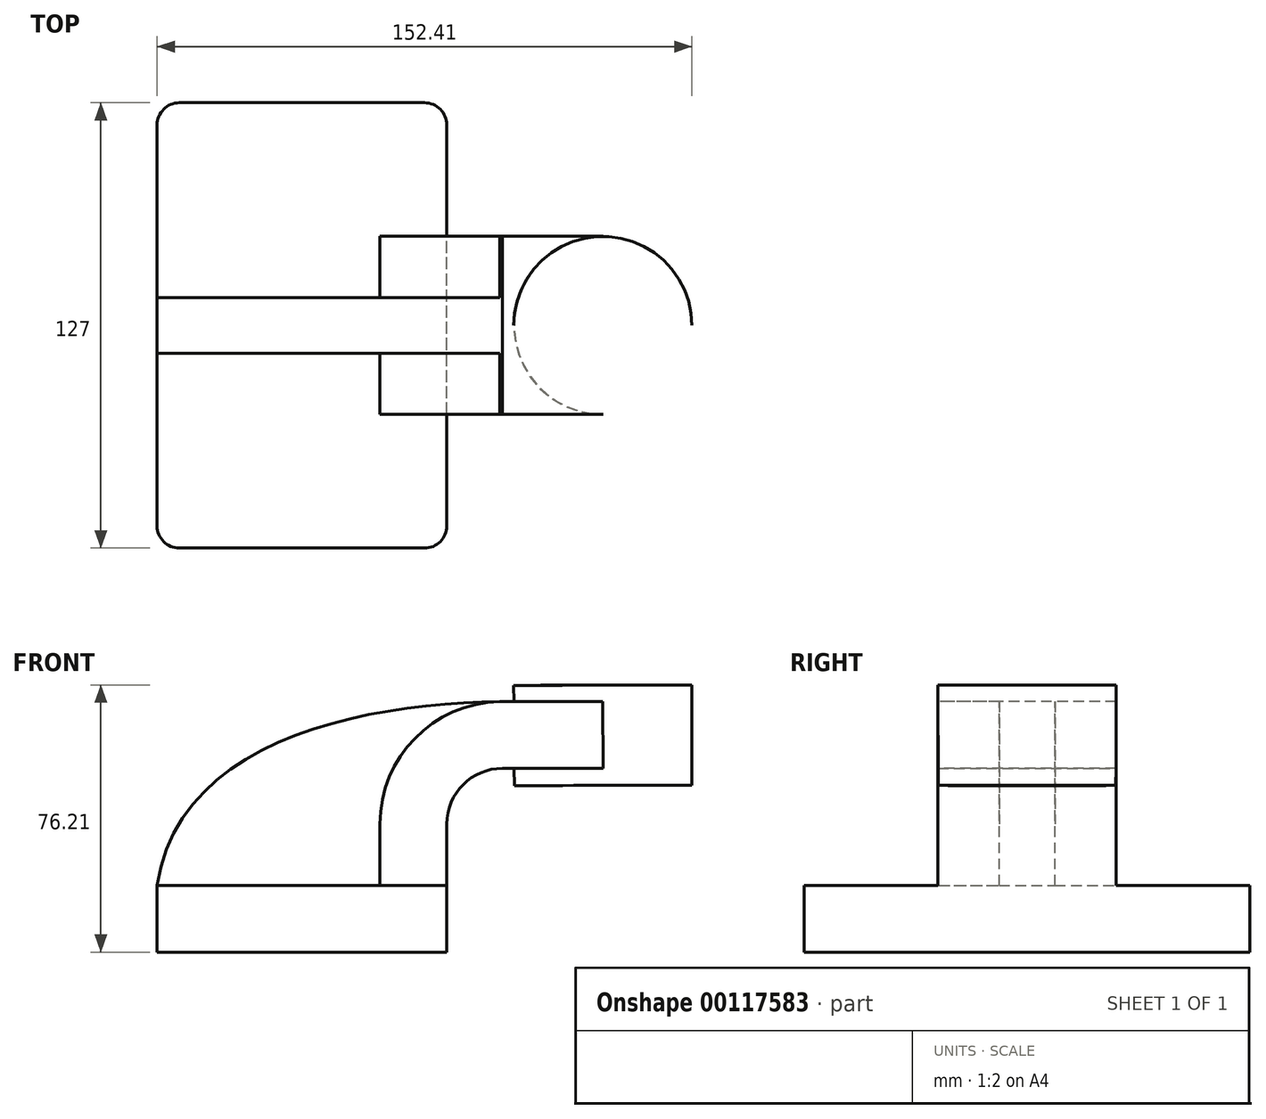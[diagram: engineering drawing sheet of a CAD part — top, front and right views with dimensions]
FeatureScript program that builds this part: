
annotation { "Feature Type Name" : "Feature", "Feature Type Description" : "" }
export const myFeature = defineFeature(function(context is Context, id is Id, definition is map)
    precondition{}
    {
        {
            var Q0;
            Q0=qCreatedBy(makeId("Front.planeOp"),FACE);
            var sketch = newSketch(context, id + "F0", { "sketchPlane" : qUnion([Q0])});
            skLineSegment(sketch, "E0.bottom", {"start": v(-41.28, -9.52) * mm, "end": v(41.28, -9.52) * mm});
            skLineSegment(sketch, "E0.top", {"start": v(-41.28, 9.52) * mm, "end": v(41.28, 9.52) * mm});
            skLineSegment(sketch, "E0.left", {"start": v(-41.28, -9.52) * mm, "end": v(-41.28, 9.52) * mm});
            skLineSegment(sketch, "E0.right", {"start": v(41.28, -9.53) * mm, "end": v(41.28, 9.52) * mm});
            skPoint(sketch, "E0.middle", {"position": v(0, 0) * mm});
            skLineSegment(sketch, "E1.bottom", {"start": v(111.12, 38.1) * mm, "end": v(60.32, 38.1) * mm});
            skLineSegment(sketch, "E1.top", {"start": v(111.12, 66.68) * mm, "end": v(60.32, 66.68) * mm});
            skLineSegment(sketch, "E1.left", {"start": v(111.12, 38.1) * mm, "end": v(111.12, 66.68) * mm});
            skLineSegment(sketch, "E1.right", {"start": v(60.32, 38.1) * mm, "end": v(60.32, 66.68) * mm});
            skPoint(sketch, "E1.middle", {"position": v(85.72, 52.39) * mm});
            skLineSegment(sketch, "E2", {"start": v(41.27, 9.52) * mm, "end": v(41.27, 27) * mm});
            skArc(sketch, "E3", {"start": v(41.27, 27) * mm, "mid": v(45.92, 38.23) * mm, "end": v(57.15, 42.88) * mm});
            skLineSegment(sketch, "E4", {"start": v(57.15, 42.88) * mm, "end": v(85.82, 42.88) * mm});
            skLineSegment(sketch, "E5.0", {"start": v(57.15, 61.93) * mm, "end": v(85.74, 61.93) * mm});
            skArc(sketch, "E5.1", {"start": v(22.23, 27) * mm, "mid": v(32.45, 51.7) * mm, "end": v(57.15, 61.93) * mm});
            skLineSegment(sketch, "E5.2", {"start": v(22.22, 9.52) * mm, "end": v(22.22, 27) * mm});
            skFitSpline(sketch, "E6", {"points": [v(-41.28, 9.53) * mm, v(57.15, 61.93) * mm], "startDerivative": vector(19.03, 126.55) * mm, "endDerivative": vector(114.8, 1.12) * mm});
            skLineSegment(sketch, "E7", {"start": v(85.72, 66.68) * mm, "end": v(85.82, 38.1) * mm});
            skPoint(sketch, "E7.endSnap0", {"position": v(85.72, 38.1) * mm});
            skSolve(sketch);
        }
        {
            var Q0;
            Q0=makeQuery(id+"F0.imprint","IMPRINT",FACE,{"disambiguationData":[TD([[makeQuery(id+"F0.imprint","IMPRINT",EDGE,{"derivedFrom":sQuery(id+"F0.wireOp",EDGE,"E0.bottom")}),1.0]])]});
            extrude(context, id + "F1", {"entities" : qUnion([Q0]), "endBound" : BoundingType.SYMMETRIC, "depth" : 127 * mm});
        }
        {
            var Q0;
            {var subQ1=sQuery(id+"F0.wireOp",EDGE,"E2");Q0=makeQuery(id+"F0.imprint","IMPRINT",FACE,{"disambiguationData":[TD([[makeQuery(id+"F0.imprint","IMPRINT",EDGE,{"derivedFrom":subQ1}),1.0]])]});}
            var Q1;
            {var subQ0=sQuery(id+"F0.wireOp",EDGE,"E4");var subQ1=sQuery(id+"F0.wireOp",EDGE,"E1.right");var subQ2=makeQuery(id+"F0.imprint","INTERSECT",VERTEX,{"derivedFrom":[subQ1,subQ0]});Q1=makeQuery(id+"F0.imprint","IMPRINT",FACE,{"disambiguationData":[TD([[makeQuery(id+"F0.imprint","IMPRINT",EDGE,{"disambiguationData":[TD([[subQ2,-1.0]])],"derivedFrom":subQ1}),-1.0]])]});}
            extrude(context, id + "F2", {"entities" : qUnion([Q0, Q1]), "operationType" : NewBodyOperationType.ADD, "endBound" : BoundingType.SYMMETRIC, "depth" : 50.8 * mm});
        }
        {
            var Q0;
            {var subQ3=sQuery(id+"F0.wireOp",EDGE,"E5.2");Q0=makeQuery(id+"F0.imprint","IMPRINT",FACE,{"disambiguationData":[TD([[makeQuery(id+"F0.imprint","IMPRINT",EDGE,{"derivedFrom":subQ3}),1.0]])]});}
            extrude(context, id + "F3", {"entities" : qUnion([Q0]), "operationType" : NewBodyOperationType.ADD, "endBound" : BoundingType.SYMMETRIC, "depth" : 15.88 * mm});
        }
        {
            var Q0;
            {var subQ4=sQuery(id+"F0.wireOp",EDGE,"E1.left");Q0=makeQuery(id+"F0.imprint","IMPRINT",FACE,{"disambiguationData":[TD([[makeQuery(id+"F0.imprint","IMPRINT",EDGE,{"derivedFrom":subQ4}),1.0]])]});}
            var Q1;
            Q1=sQuery(id+"F0.wireOp",EDGE,"E7");
            revolve(context, id + "F4", {"operationType" : NewBodyOperationType.ADD, "entities" : qUnion([Q0]), "axis" : qUnion([Q1]), "revolveType" : RevolveType.FULL});
        }
        {
            var Q0;
            Q0=makeQuery(id+"F1.opExtrude","CAP_EDGE",EDGE,{"disambiguationData":[OSD([sQuery(id+"F0.wireOp",EDGE,"E0.right")])],"isStart":false});
            var Q1;
            Q1=makeQuery(id+"F1.opExtrude","CAP_EDGE",EDGE,{"disambiguationData":[OSD([sQuery(id+"F0.wireOp",EDGE,"E0.right")])],"isStart":true});
            var Q2;
            Q2=makeQuery(id+"F1.opExtrude","CAP_EDGE",EDGE,{"disambiguationData":[OSD([sQuery(id+"F0.wireOp",EDGE,"E0.left")])],"isStart":false});
            var Q3;
            Q3=makeQuery(id+"F1.opExtrude","CAP_EDGE",EDGE,{"disambiguationData":[OSD([sQuery(id+"F0.wireOp",EDGE,"E0.left")])],"isStart":true});
            fillet(context, id + "F5", {"entities" : qUnion([Q0, Q1, Q2, Q3]), "radius" : 6.35 * mm, "tangentPropagation" : true, "allowEdgeOverflow" : false});
        }
    });
